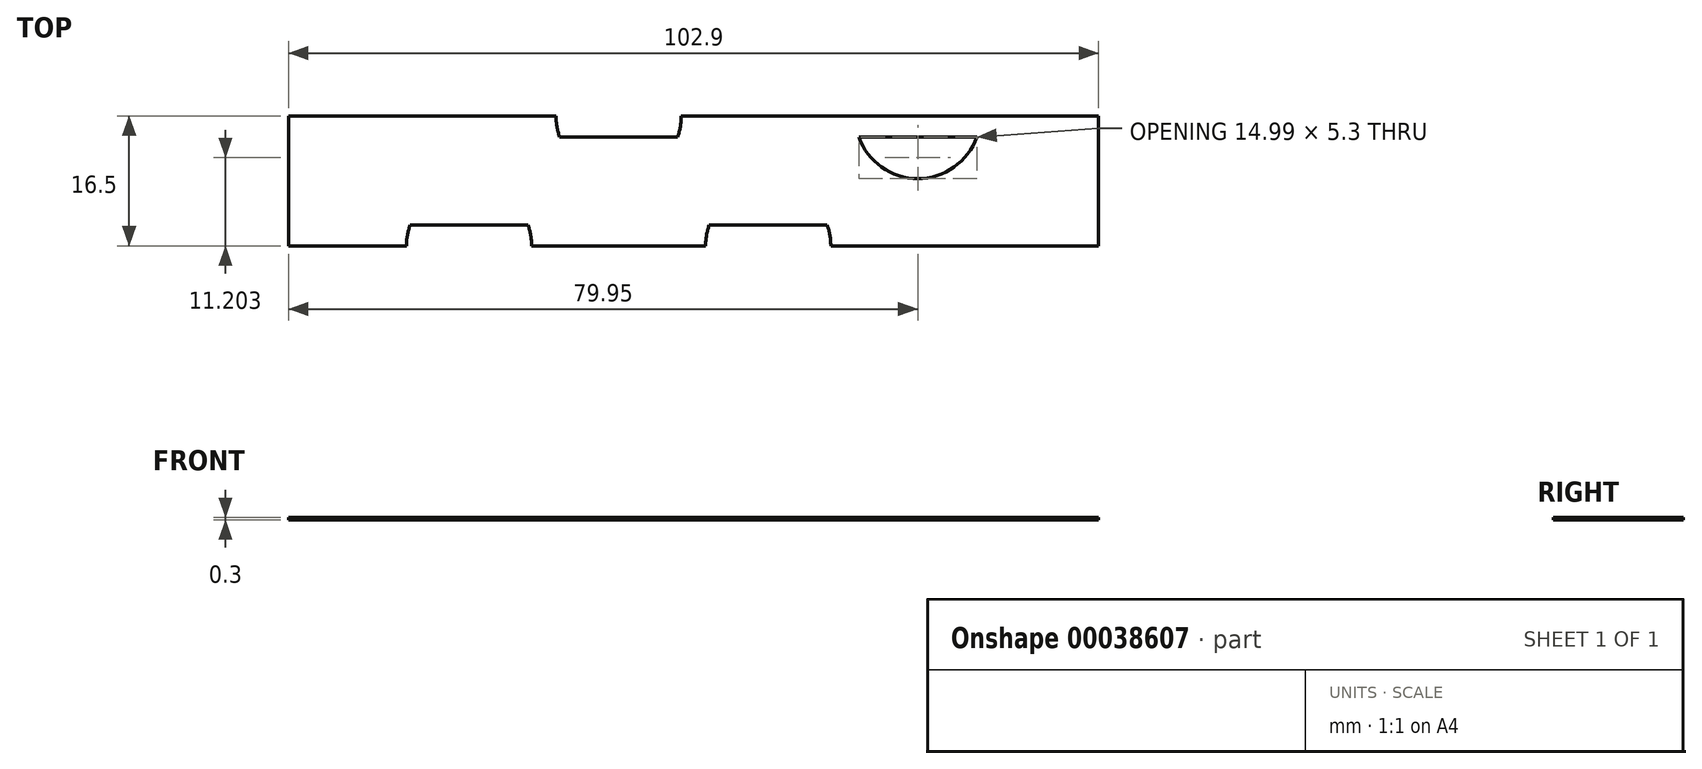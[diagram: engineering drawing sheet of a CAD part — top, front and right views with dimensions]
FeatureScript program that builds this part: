
annotation { "Feature Type Name" : "Feature", "Feature Type Description" : "" }
export const myFeature = defineFeature(function(context is Context, id is Id, definition is map)
    precondition{}
    {
        {
            var Q0;
            Q0=qCreatedBy(makeId("Top.planeOp"),FACE);
            var sketch = newSketch(context, id + "F0", { "sketchPlane" : qUnion([Q0])});
            skLineSegment(sketch, "E0.bottom", {"start": v(0, -8.18) * mm, "end": v(102.9, -8.18) * mm});
            skLineSegment(sketch, "E0.top", {"start": v(0, 8.32) * mm, "end": v(102.9, 8.32) * mm});
            skLineSegment(sketch, "E0.left", {"start": v(0, -8.18) * mm, "end": v(0, 8.32) * mm});
            skLineSegment(sketch, "E0.right", {"start": v(102.9, -8.18) * mm, "end": v(102.9, 8.32) * mm});
            skCircle(sketch, "E1", {"center": v(22.95, -8.18) * mm, "radius": 7.95 * mm});
            skCircle(sketch, "E2", {"center": v(41.95, 8.32) * mm, "radius": 7.95 * mm});
            skCircle(sketch, "E3", {"center": v(60.95, -8.18) * mm, "radius": 7.95 * mm});
            skCircle(sketch, "E4", {"center": v(79.95, 8.32) * mm, "radius": 7.95 * mm});
            skLineSegment(sketch, "E5", {"start": v(15.45, -5.53) * mm, "end": v(30.45, -5.53) * mm});
            skLineSegment(sketch, "E6", {"start": v(34.45, 5.67) * mm, "end": v(49.45, 5.67) * mm});
            skLineSegment(sketch, "E7", {"start": v(53.45, -5.53) * mm, "end": v(68.45, -5.53) * mm});
            skLineSegment(sketch, "E8", {"start": v(72.4, 5.67) * mm, "end": v(87.45, 5.67) * mm});
            skSolve(sketch);
        }
        {
            var Q0;
            {var subQ5=sQuery(id+"F0.wireOp",EDGE,"E0.left");Q0=makeQuery(id+"F0.imprint","IMPRINT",FACE,{"disambiguationData":[TD([[makeQuery(id+"F0.imprint","IMPRINT",EDGE,{"derivedFrom":subQ5}),-1.0]])]});}
            var Q1;
            {var subQ0=sQuery(id+"F0.wireOp",EDGE,"E5");Q1=makeQuery(id+"F0.imprint","IMPRINT",FACE,{"disambiguationData":[TD([[makeQuery(id+"F0.imprint","IMPRINT",EDGE,{"derivedFrom":subQ0}),1.0]])]});}
            var Q2;
            {var subQ0=sQuery(id+"F0.wireOp",EDGE,"E6");Q2=makeQuery(id+"F0.imprint","IMPRINT",FACE,{"disambiguationData":[TD([[makeQuery(id+"F0.imprint","IMPRINT",EDGE,{"derivedFrom":subQ0}),-1.0]])]});}
            var Q3;
            {var subQ0=sQuery(id+"F0.wireOp",EDGE,"E7");Q3=makeQuery(id+"F0.imprint","IMPRINT",FACE,{"disambiguationData":[TD([[makeQuery(id+"F0.imprint","IMPRINT",EDGE,{"derivedFrom":subQ0}),1.0]])]});}
            var Q4;
            {var subQ0=sQuery(id+"F0.wireOp",EDGE,"E8");var subQ1=sQuery(id+"F0.wireOp",EDGE,"E4");var subQ2=makeQuery(id+"F0.imprint","INTERSECT",VERTEX,{"disambiguationData":[OD(0.0)],"derivedFrom":[subQ1,subQ0]});Q4=makeQuery(id+"F0.imprint","IMPRINT",FACE,{"disambiguationData":[TD([[makeQuery(id+"F0.imprint","IMPRINT",EDGE,{"disambiguationData":[TD([[subQ2,1.0]])],"derivedFrom":subQ1}),1.0]])]});}
            extrude(context, id + "F1", {"entities" : qUnion([Q0, Q1, Q2, Q3, Q4]), "depth" : 0.3 * mm});
        }
    });
